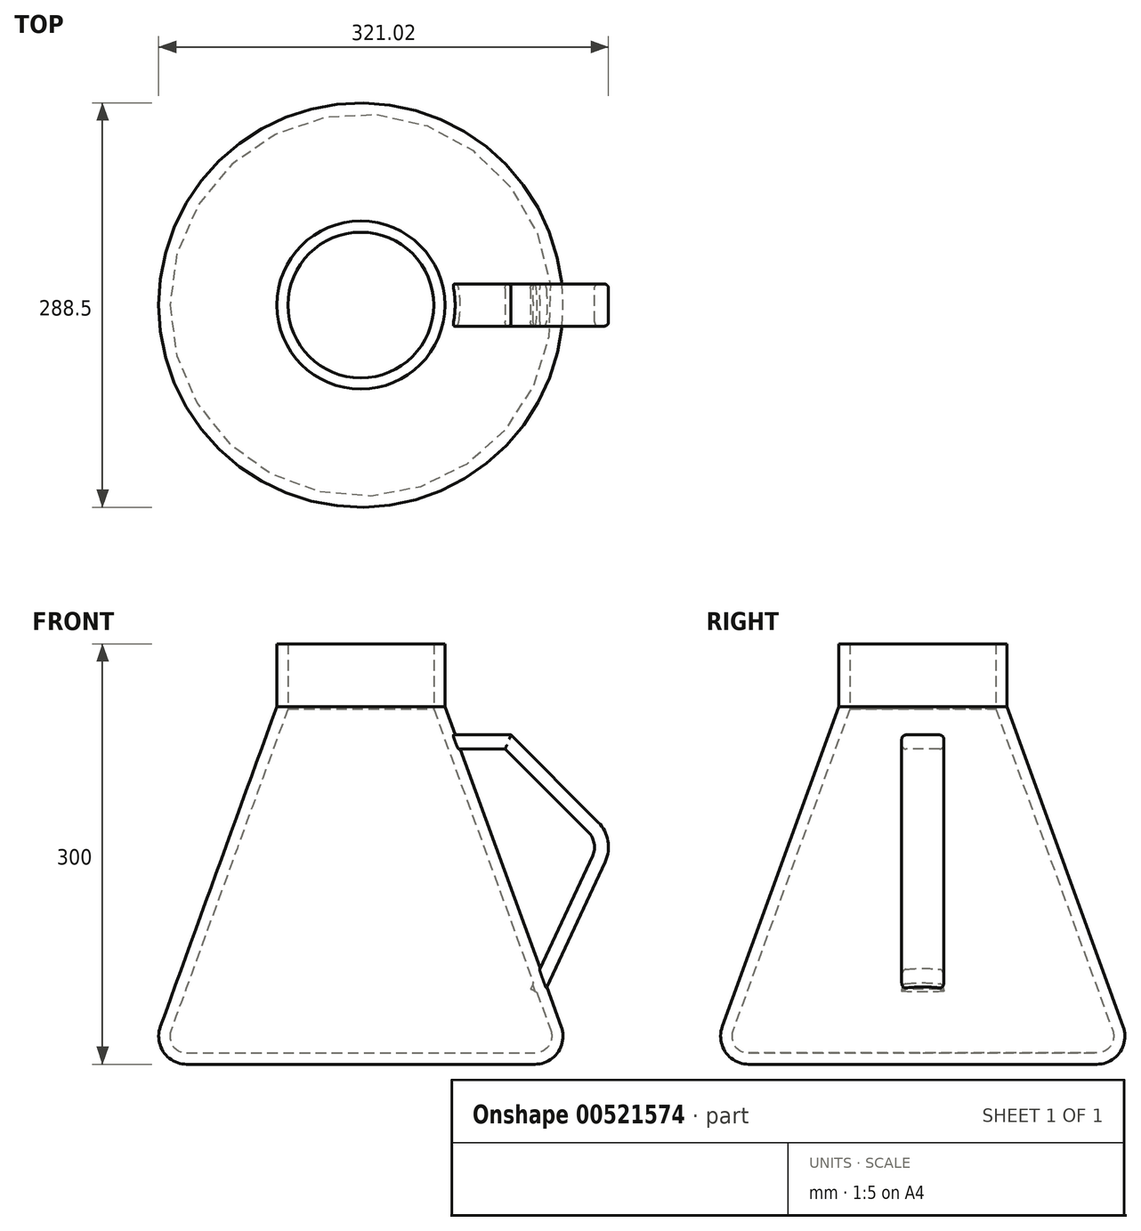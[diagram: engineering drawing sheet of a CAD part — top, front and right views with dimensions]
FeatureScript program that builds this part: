
annotation { "Feature Type Name" : "Feature", "Feature Type Description" : "" }
export const myFeature = defineFeature(function(context is Context, id is Id, definition is map)
    precondition{}
    {
        {
            var Q0;
            Q0=qCreatedBy(makeId("Front.planeOp"),FACE);
            var sketch = newSketch(context, id + "F0", { "sketchPlane" : qUnion([Q0])});
            skLineSegment(sketch, "E0", {"start": v(0, 0) * mm, "end": v(124.25, 0) * mm});
            skLineSegment(sketch, "E1", {"start": v(143.04, 26.84) * mm, "end": v(60, 255) * mm});
            skLineSegment(sketch, "E2", {"start": v(60, 255) * mm, "end": v(60, 255) * mm});
            skPoint(sketch, "E3.visualSharp", {"position": v(152.81, 0) * mm});
            skArc(sketch, "E3.filletArc", {"start": v(124.25, 0) * mm, "mid": v(140.63, 8.53) * mm, "end": v(143.04, 26.84) * mm});
            skLineSegment(sketch, "E4", {"start": v(0, 0) * mm, "end": v(0, 300) * mm, "construction": true});
            skLineSegment(sketch, "E5", {"start": v(52, 300) * mm, "end": v(60, 300) * mm});
            skLineSegment(sketch, "E6", {"start": v(60, 300) * mm, "end": v(60, 255) * mm});
            skLineSegment(sketch, "E7.1", {"start": v(0, 8) * mm, "end": v(124.25, 8) * mm});
            skArc(sketch, "E7.2", {"start": v(124.25, 8) * mm, "mid": v(134.08, 13.12) * mm, "end": v(135.53, 24.1) * mm});
            skLineSegment(sketch, "E7.3", {"start": v(135.53, 24.1) * mm, "end": v(52, 253.59) * mm});
            skLineSegment(sketch, "E7.4", {"start": v(52, 300) * mm, "end": v(52, 253.59) * mm});
            skLineSegment(sketch, "E8", {"start": v(0, 8) * mm, "end": v(0, 0) * mm});
            skSolve(sketch);
        }
        {
            var Q0;
            Q0=makeQuery(id+"F0.imprint","IMPRINT",FACE,{"disambiguationData":[TD([[makeQuery(id+"F0.imprint","IMPRINT",EDGE,{"derivedFrom":sQuery(id+"F0.wireOp",EDGE,"E0")}),1.0]])]});
            var Q1;
            Q1=sQuery(id+"F0.wireOp",EDGE,"E4");
            revolve(context, id + "F1", {"entities" : qUnion([Q0]), "axis" : qUnion([Q1]), "revolveType" : RevolveType.FULL});
        }
        {
            var Q0;
            Q0=qCreatedBy(makeId("Right.planeOp"),FACE);
            var sketch = newSketch(context, id + "F2", { "sketchPlane" : qUnion([Q0])});
            skLineSegment(sketch, "E9.bottom", {"start": v(12, 225) * mm, "end": v(-12, 225) * mm});
            skLineSegment(sketch, "E9.top", {"start": v(12, 235) * mm, "end": v(-12, 235) * mm});
            skLineSegment(sketch, "E9.left", {"start": v(15, 228) * mm, "end": v(15, 232) * mm});
            skLineSegment(sketch, "E9.right", {"start": v(-15, 228) * mm, "end": v(-15, 232) * mm});
            skPoint(sketch, "E9.middle", {"position": v(0, 230) * mm});
            skPoint(sketch, "E10.visualSharp", {"position": v(-15, 235) * mm});
            skArc(sketch, "E10.filletArc", {"start": v(-12, 235) * mm, "mid": v(-14.12, 234.12) * mm, "end": v(-15, 232) * mm});
            skPoint(sketch, "E11.visualSharp", {"position": v(15, 235) * mm});
            skArc(sketch, "E11.filletArc", {"start": v(15, 232) * mm, "mid": v(14.12, 234.12) * mm, "end": v(12, 235) * mm});
            skPoint(sketch, "E12.visualSharp", {"position": v(15, 225) * mm});
            skArc(sketch, "E12.filletArc", {"start": v(12, 225) * mm, "mid": v(14.12, 225.88) * mm, "end": v(15, 228) * mm});
            skPoint(sketch, "E13.visualSharp", {"position": v(-15, 225) * mm});
            skArc(sketch, "E13.filletArc", {"start": v(-15, 228) * mm, "mid": v(-14.12, 225.88) * mm, "end": v(-12, 225) * mm});
            skSolve(sketch);
        }
        {
            var Q0;
            Q0=qCreatedBy(makeId("Front.planeOp"),FACE);
            var sketch = newSketch(context, id + "F3", { "sketchPlane" : qUnion([Q0])});
            skLineSegment(sketch, "E14", {"start": v(0, 230) * mm, "end": v(105.1, 230) * mm});
            skLineSegment(sketch, "E15", {"start": v(105.1, 230) * mm, "end": v(165.9, 169.2) * mm});
            skLineSegment(sketch, "E16", {"start": v(169.9, 146.6) * mm, "end": v(125.55, 51.5) * mm});
            skLineSegment(sketch, "E17", {"start": v(60, 255) * mm, "end": v(143.04, 26.84) * mm});
            skLineSegment(sketch, "E18", {"start": v(60, 255) * mm, "end": v(143.04, 26.84) * mm, "construction": true});
            skPoint(sketch, "E19", {"position": v(69.1, 230) * mm});
            skPoint(sketch, "E20.visualSharp", {"position": v(175.8, 159.29) * mm});
            skArc(sketch, "E20.filletArc", {"start": v(169.9, 146.6) * mm, "mid": v(171.46, 158.52) * mm, "end": v(165.9, 169.2) * mm});
            skLineSegment(sketch, "E21.0", {"start": v(52.48, 252.26) * mm, "end": v(135.53, 24.1) * mm, "construction": true});
            skSolve(sketch);
        }
        {
            var Q0;
            Q0=makeQuery(id+"F2.imprint","IMPRINT",FACE,{"disambiguationData":[TD([[makeQuery(id+"F2.imprint","IMPRINT",EDGE,{"derivedFrom":sQuery(id+"F2.wireOp",EDGE,"E9.bottom")}),-1.0]])]});
            var Q1;
            Q1=sQuery(id+"F3.wireOp",EDGE,"E14");
            var Q2;
            Q2=sQuery(id+"F3.wireOp",EDGE,"E15");
            var Q3;
            Q3=sQuery(id+"F3.wireOp",EDGE,"E20.filletArc");
            var Q4;
            Q4=sQuery(id+"F3.wireOp",EDGE,"E16");
            sweep(context, id + "F4", {"operationType" : NewBodyOperationType.ADD, "profiles" : qUnion([Q0]), "path" : qUnion([Q1, Q2, Q3, Q4])});
        }
        {
            var Q0;
            Q0=makeQuery(id+"F4.opSweep","CAP_FACE",FACE,{"disambiguationData":[OSD([sQuery(id+"F2.wireOp",EDGE,"E9.bottom"),sQuery(id+"F2.wireOp",EDGE,"E9.top"),sQuery(id+"F2.wireOp",EDGE,"E9.left"),sQuery(id+"F2.wireOp",EDGE,"E9.right"),sQuery(id+"F2.wireOp",EDGE,"E10.filletArc"),sQuery(id+"F2.wireOp",EDGE,"E11.filletArc"),sQuery(id+"F2.wireOp",EDGE,"E12.filletArc"),sQuery(id+"F2.wireOp",EDGE,"E13.filletArc"),sQuery(id+"F3.wireOp",VERTEX,"E14.start")])],"isStart":true});
            var sketch = newSketch(context, id + "F5", { "sketchPlane" : qUnion([Q0])});
            skArc(sketch, "E22.0.0", {"start": v(-12, 235) * mm, "mid": v(-14.12, 234.12) * mm, "end": v(-15, 232) * mm});
            skLineSegment(sketch, "E22.0.1", {"start": v(-15, 232) * mm, "end": v(-15, 228) * mm});
            skArc(sketch, "E22.0.2", {"start": v(-15, 228) * mm, "mid": v(-14.12, 225.88) * mm, "end": v(-12, 225) * mm});
            skLineSegment(sketch, "E22.0.3", {"start": v(12, 225) * mm, "end": v(-12, 225) * mm});
            skArc(sketch, "E22.0.4", {"start": v(12, 225) * mm, "mid": v(14.12, 225.88) * mm, "end": v(15, 228) * mm});
            skLineSegment(sketch, "E22.0.5", {"start": v(15, 232) * mm, "end": v(15, 228) * mm});
            skArc(sketch, "E22.0.6", {"start": v(15, 232) * mm, "mid": v(14.12, 234.12) * mm, "end": v(12, 235) * mm});
            skLineSegment(sketch, "E22.0.7", {"start": v(12, 235) * mm, "end": v(-12, 235) * mm});
            skSolve(sketch);
        }
        {
            var Q0;
            Q0 = qSketchRegion(id + "F5", true);
            var Q1;
            Q1=makeQuery(id+"F1.opRevolve","SWEPT_FACE",FACE,{"disambiguationData":[OSD([sQuery(id+"F0.wireOp",EDGE,"E7.3")])]});
            extrude(context, id + "F6", {"entities" : qUnion([Q0]), "operationType" : NewBodyOperationType.REMOVE, "endBound" : BoundingType.UP_TO_SURFACE, "oppositeDirection" : true, "depth" : 25 * mm, "endBoundEntityFace" : qUnion([Q1]), "offsetDistance" : 25 * mm});
        }
    });
